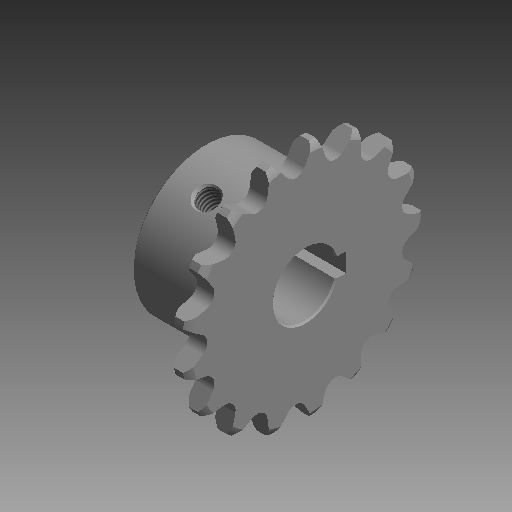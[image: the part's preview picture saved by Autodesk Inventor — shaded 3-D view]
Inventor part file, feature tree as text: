
AUTODESK INVENTOR PART (.ipt)
format: ipt  version: 2019 (Build 230136000, 136)  size: 330,752 bytes
history: native  units: mm (DEFAULTED — no unit token found)
features: sketch x5, revolve x3, extrude x2, thread x2
ambient origin geometry x8: Origin, YZ Plane, XZ Plane, XY Plane, X Axis, Y Axis, Z Axis, Center Point
bodies: Solid1 (feature_tree), body_XY (feature_tree), body_YZ (feature_tree), body_ZX (feature_tree), body_X (feature_tree), body_Y (feature_tree), body_Z (feature_tree), body_Center (feature_tree)
feature tree (12):
  revolve  "Revolution1"  [1 undecoded]
  extrude  "Extrusion1"  Depth=4.721mm TaperAngle=0.0deg
  revolve  "Revolution2"  [1 undecoded]
  thread  "Thread1"  [1 undecoded]
  revolve  "Revolution3"  [1 undecoded]
  thread  "Thread2"  [1 undecoded]
  extrude  "Extrusion2"  [1 undecoded]
  sketch  "Sketch_1"  dims[d0=360.0deg d1=3.2mm d2=0.0mm]
  sketch  "Sketch_7"
  sketch  "Sketch_2"  dims[d3=360.0deg d4=4.721mm d5=0.0mm]
  sketch  "Sketch_3"  dims[d6=360.0deg d7=4.721mm d8=0.0mm d9=16.0mm d10=0.0mm]
  sketch  "Sketch_4"  dims[d11=0.0mm]
note: 6 required parameter values undecoded (feature->parameter linkage not recoverable at this tier; creation-order binding heuristic only, values carry confidence <= 0.55)